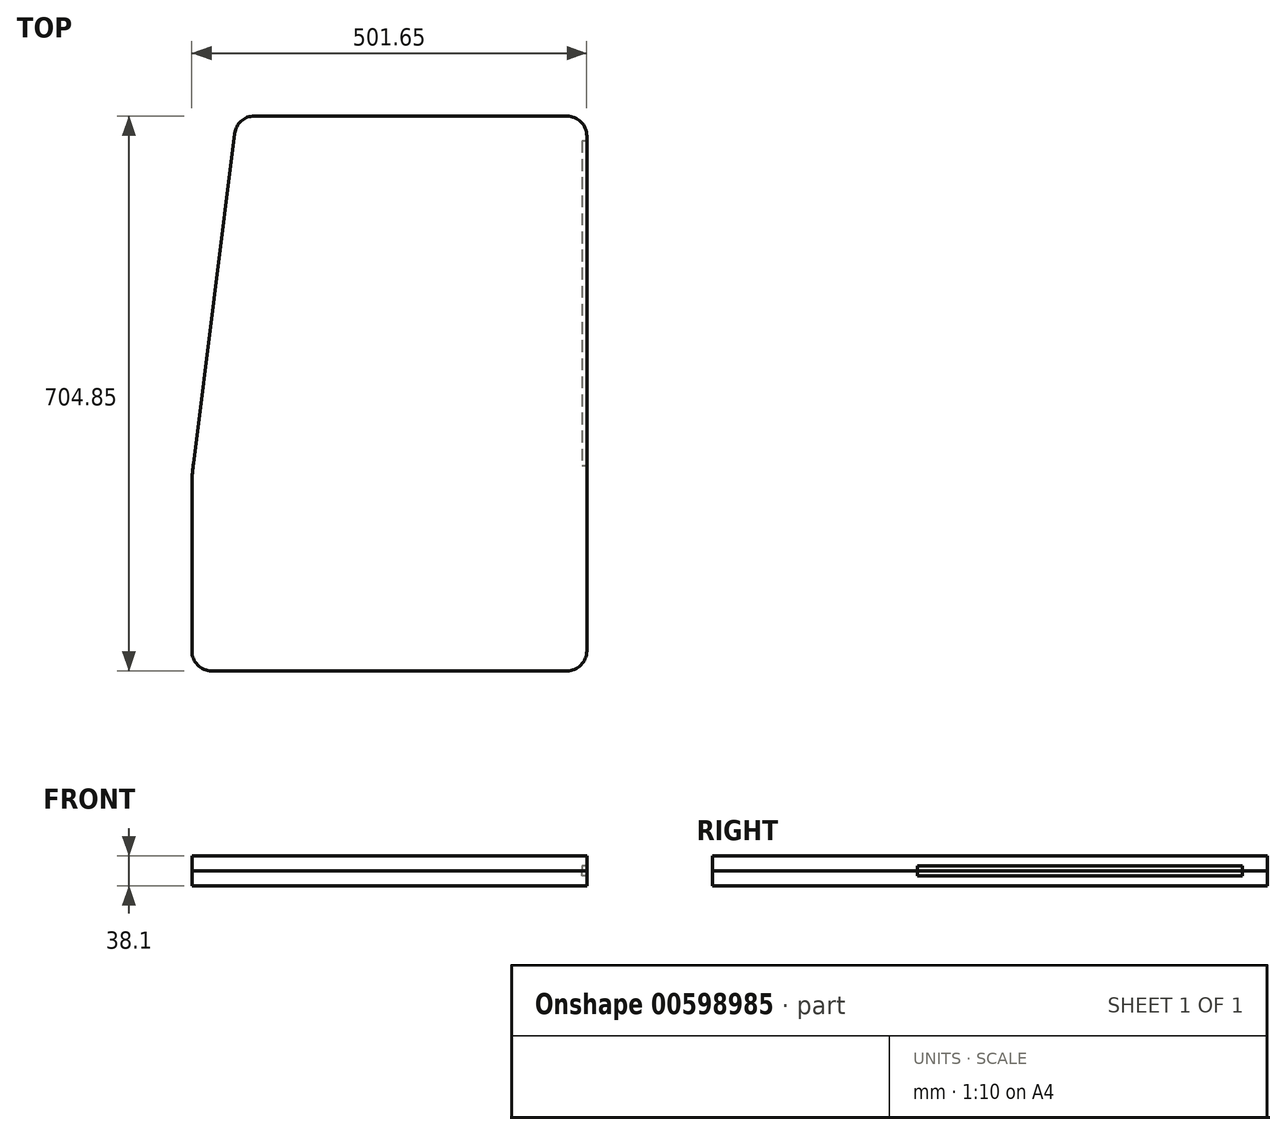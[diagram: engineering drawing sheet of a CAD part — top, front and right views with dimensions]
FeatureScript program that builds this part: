
annotation { "Feature Type Name" : "Feature", "Feature Type Description" : "" }
export const myFeature = defineFeature(function(context is Context, id is Id, definition is map)
    precondition{}
    {
        {
            var Q0;
            Q0=qCreatedBy(makeId("Top.planeOp"),FACE);
            var sketch = newSketch(context, id + "F0", { "sketchPlane" : qUnion([Q0])});
            skLineSegment(sketch, "E0", {"start": v(50.6, 16.84) * mm, "end": v(501.45, 16.84) * mm});
            skLineSegment(sketch, "E1", {"start": v(526.85, 42.24) * mm, "end": v(526.85, 696.3) * mm});
            skLineSegment(sketch, "E2", {"start": v(501.45, 721.7) * mm, "end": v(104.78, 721.7) * mm});
            skLineSegment(sketch, "E3", {"start": v(25.2, 42.24) * mm, "end": v(25.2, 248.68) * mm});
            skLineSegment(sketch, "E4", {"start": v(27.17, 280.19) * mm, "end": v(79.57, 699.44) * mm});
            skPoint(sketch, "E5.visualSharp", {"position": v(526.85, 16.84) * mm});
            skArc(sketch, "E5.filletArc", {"start": v(501.45, 16.84) * mm, "mid": v(519.41, 24.28) * mm, "end": v(526.85, 42.24) * mm});
            skPoint(sketch, "E6.visualSharp", {"position": v(526.85, 721.7) * mm});
            skArc(sketch, "E6.filletArc", {"start": v(526.85, 696.3) * mm, "mid": v(519.41, 714.25) * mm, "end": v(501.45, 721.7) * mm});
            skPoint(sketch, "E7.visualSharp", {"position": v(82.35, 721.7) * mm});
            skArc(sketch, "E7.filletArc", {"start": v(104.78, 721.7) * mm, "mid": v(87.97, 715.34) * mm, "end": v(79.57, 699.44) * mm});
            skPoint(sketch, "E8.visualSharp", {"position": v(25.2, 16.84) * mm});
            skArc(sketch, "E8.filletArc", {"start": v(25.2, 42.24) * mm, "mid": v(32.64, 24.28) * mm, "end": v(50.6, 16.84) * mm});
            skPoint(sketch, "E9.visualSharp", {"position": v(25.2, 264.5) * mm});
            skArc(sketch, "E9.filletArc", {"start": v(27.17, 280.19) * mm, "mid": v(25.7, 264.46) * mm, "end": v(25.2, 248.68) * mm});
            skSolve(sketch);
        }
        {
            var Q0;
            Q0 = qSketchRegion(id + "F0", true);
            extrude(context, id + "F1", {"entities" : qUnion([Q0]), "depth" : 19.05 * mm, "offsetDistance" : 25.4 * mm});
        }
        {
            var Q0;
            Q0=makeQuery(id+"F1.opExtrude","CAP_FACE",FACE,{"disambiguationData":[OSD([sQuery(id+"F0.wireOp",EDGE,"E0"),sQuery(id+"F0.wireOp",EDGE,"E1"),sQuery(id+"F0.wireOp",EDGE,"E2"),sQuery(id+"F0.wireOp",EDGE,"E3"),sQuery(id+"F0.wireOp",EDGE,"E4")])],"isStart":true});
            var sketch = newSketch(context, id + "F2", { "sketchPlane" : qUnion([Q0])});
            skLineSegment(sketch, "E10.bottom", {"start": v(526.85, -689.94) * mm, "end": v(520.5, -689.94) * mm});
            skLineSegment(sketch, "E10.top", {"start": v(526.85, -277.2) * mm, "end": v(520.5, -277.2) * mm});
            skLineSegment(sketch, "E10.left", {"start": v(526.85, -689.94) * mm, "end": v(526.85, -277.2) * mm});
            skLineSegment(sketch, "E10.right", {"start": v(520.5, -689.94) * mm, "end": v(520.5, -277.2) * mm});
            skSolve(sketch);
        }
        {
            var Q0;
            Q0 = qSketchRegion(id + "F2", true);
            extrude(context, id + "F3", {"entities" : qUnion([Q0]), "operationType" : NewBodyOperationType.REMOVE, "oppositeDirection" : true, "depth" : 6.35 * mm, "offsetDistance" : 25.4 * mm});
        }
        {
            var Q0;
            Q0=makeQuery(id+"F1.opExtrude","SWEPT_BODY",BODY,{"disambiguationData":[OSD([sQuery(id+"F0.wireOp",EDGE,"E0"),sQuery(id+"F0.wireOp",EDGE,"E1"),sQuery(id+"F0.wireOp",EDGE,"E2"),sQuery(id+"F0.wireOp",EDGE,"E3"),sQuery(id+"F0.wireOp",EDGE,"E4"),sQuery(id+"F0.wireOp",EDGE,"E5.filletArc"),sQuery(id+"F0.wireOp",EDGE,"E6.filletArc"),sQuery(id+"F0.wireOp",EDGE,"E7.filletArc"),sQuery(id+"F0.wireOp",EDGE,"E8.filletArc"),sQuery(id+"F0.wireOp",EDGE,"E9.filletArc")])]});
            var Q1;
            Q1=qCreatedBy(makeId("Top.planeOp"),FACE);
            mirror(context, id + "F4", {"entities" : qUnion([Q0]), "mirrorPlane" : qUnion([Q1])});
        }
    });
